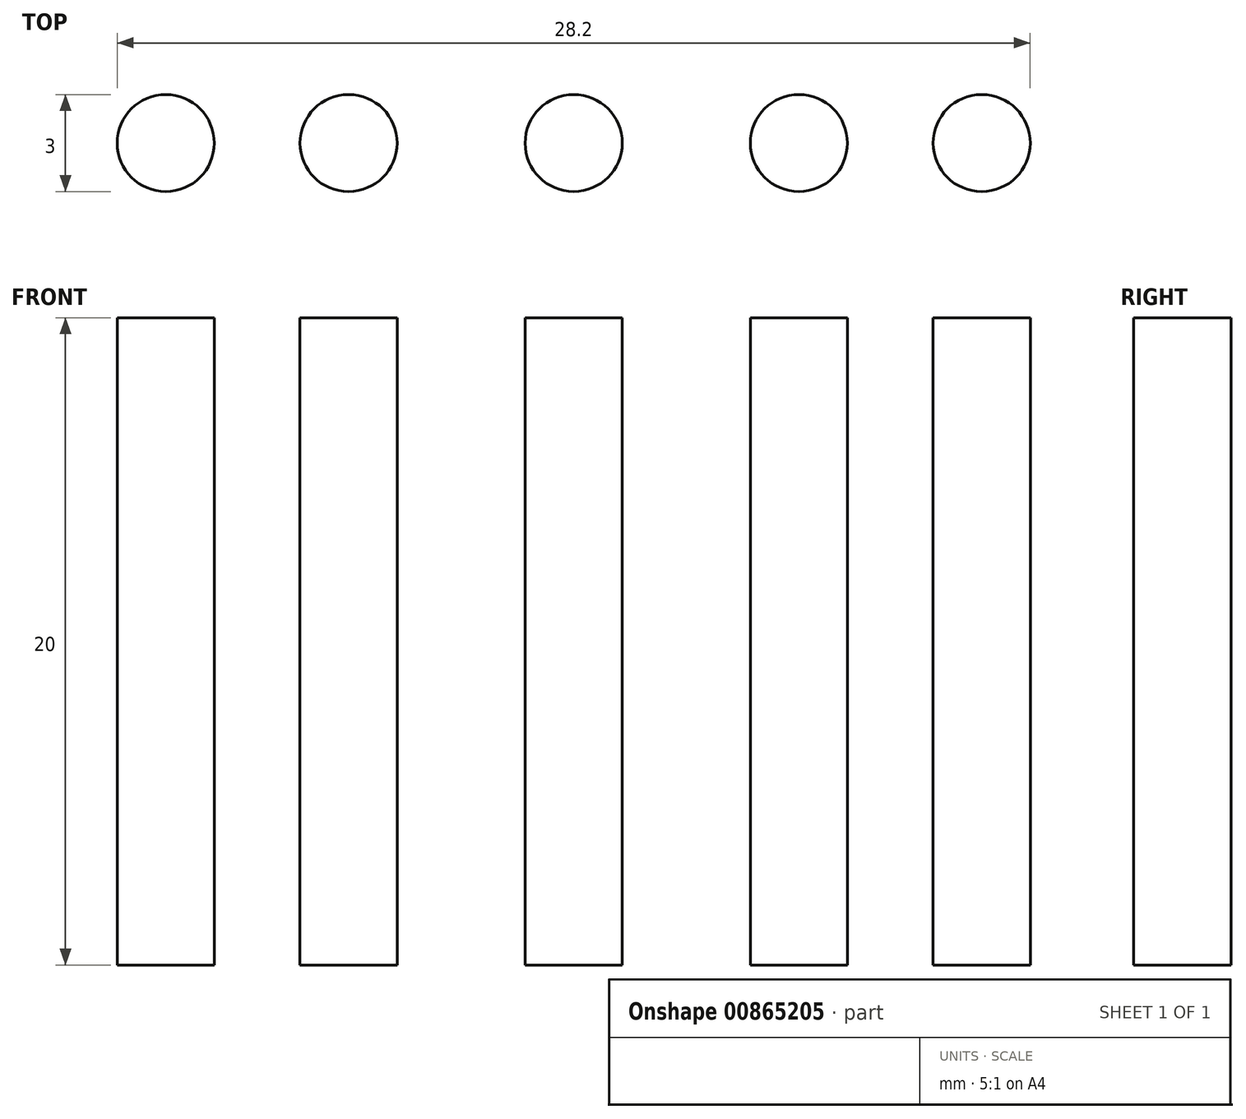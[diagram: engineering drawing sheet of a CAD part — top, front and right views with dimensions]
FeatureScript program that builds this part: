
annotation { "Feature Type Name" : "Feature", "Feature Type Description" : "" }
export const myFeature = defineFeature(function(context is Context, id is Id, definition is map)
    precondition{}
    {
        {
            var Q0;
            Q0=qCreatedBy(makeId("Top.planeOp"),FACE);
            var sketch = newSketch(context, id + "F0", { "sketchPlane" : qUnion([Q0])});
            skCircle(sketch, "E0", {"center": v(0, 0) * mm, "radius": 1.5 * mm});
            skCircle(sketch, "E1", {"center": v(6.95, 0) * mm, "radius": 1.5 * mm});
            skCircle(sketch, "E2", {"center": v(12.6, 0) * mm, "radius": 1.5 * mm});
            skCircle(sketch, "E3.MirrorC", {"center": v(-6.95, 0) * mm, "radius": 1.5 * mm});
            skCircle(sketch, "E4.MirrorC", {"center": v(-12.6, 0) * mm, "radius": 1.5 * mm});
            skSolve(sketch);
        }
        {
            var Q0;
            Q0=qSketchRegion(id+"F0",true);
            extrude(context, id + "F1", {"entities" : qUnion([Q0]), "depth" : 20 * mm, "offsetDistance" : 25 * mm});
        }
    });
